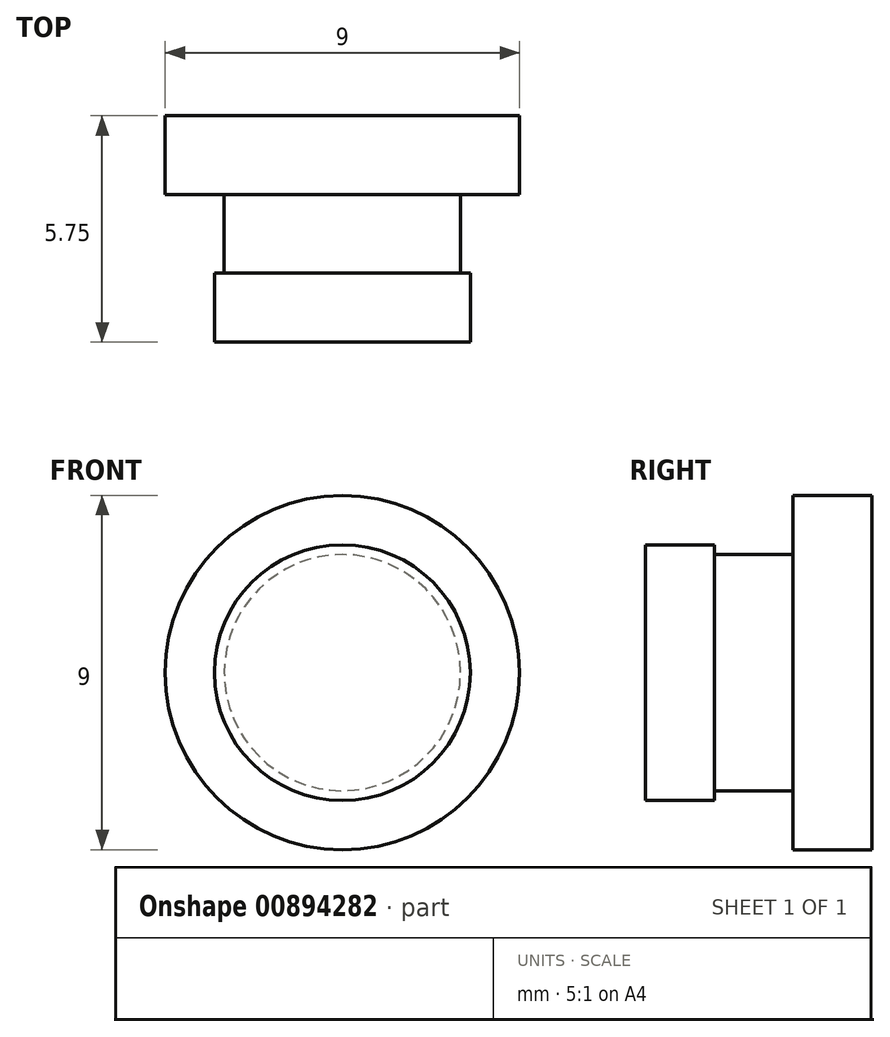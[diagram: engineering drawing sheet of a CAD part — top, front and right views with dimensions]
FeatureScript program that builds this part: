
annotation { "Feature Type Name" : "Feature", "Feature Type Description" : "" }
export const myFeature = defineFeature(function(context is Context, id is Id, definition is map)
    precondition{}
    {
        {
            var Q0;
            Q0=qCreatedBy(makeId("Right.planeOp"),FACE);
            var sketch = newSketch(context, id + "F0", { "sketchPlane" : qUnion([Q0])});
            skLineSegment(sketch, "E0", {"start": v(0, 0) * mm, "end": v(0, 3.25) * mm});
            skLineSegment(sketch, "E1", {"start": v(0, 3.25) * mm, "end": v(1.75, 3.25) * mm});
            skLineSegment(sketch, "E2", {"start": v(1.75, 3.25) * mm, "end": v(1.75, 3) * mm});
            skLineSegment(sketch, "E3", {"start": v(1.75, 3) * mm, "end": v(3.75, 3) * mm});
            skLineSegment(sketch, "E4", {"start": v(3.75, 3) * mm, "end": v(3.75, 4.5) * mm});
            skLineSegment(sketch, "E5", {"start": v(3.75, 4.5) * mm, "end": v(5.75, 4.5) * mm});
            skLineSegment(sketch, "E6", {"start": v(5.75, 4.5) * mm, "end": v(5.75, 0) * mm});
            skLineSegment(sketch, "E7", {"start": v(5.75, 0) * mm, "end": v(0, 0) * mm});
            skSolve(sketch);
        }
        {
            var Q0;
            Q0=makeQuery(id+"F0.imprint","IMPRINT",FACE,{"disambiguationData":[TD([[makeQuery(id+"F0.imprint","IMPRINT",EDGE,{"derivedFrom":sQuery(id+"F0.wireOp",EDGE,"E0")}),-1.0]])]});
            var Q1;
            Q1=sQuery(id+"F0.wireOp",EDGE,"E7");
            revolve(context, id + "F1", {"surfaceOperationType" : NewSurfaceOperationType.NEW, "entities" : qUnion([Q0]), "axis" : qUnion([Q1]), "revolveType" : RevolveType.FULL});
        }
    });
